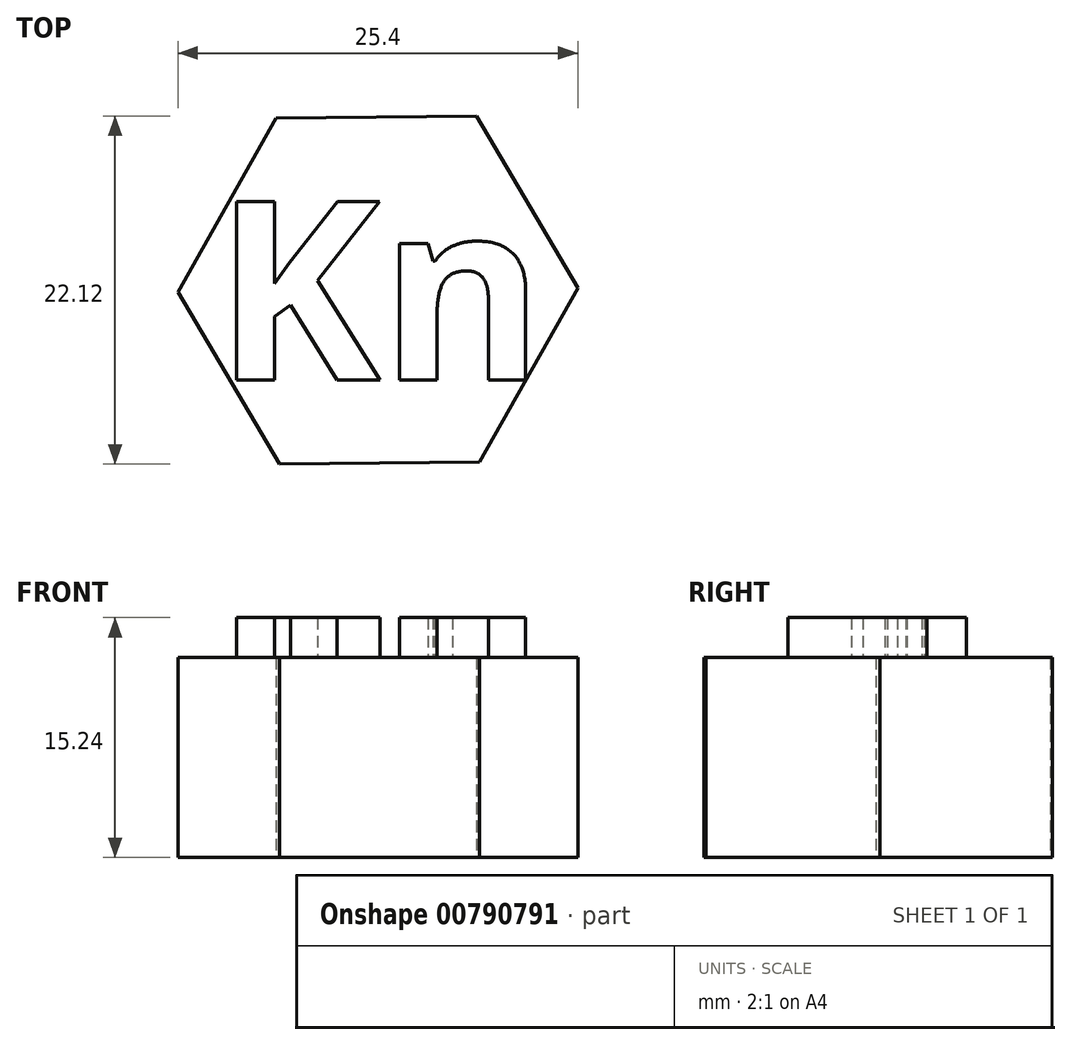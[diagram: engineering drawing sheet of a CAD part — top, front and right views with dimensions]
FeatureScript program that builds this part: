
annotation { "Feature Type Name" : "Feature", "Feature Type Description" : "" }
export const myFeature = defineFeature(function(context is Context, id is Id, definition is map)
    precondition{}
    {
        {
            var Q0;
            Q0=qCreatedBy(makeId("Top.planeOp"),FACE);
            var sketch = newSketch(context, id + "F0", { "sketchPlane" : qUnion([Q0])});
            skCircle(sketch, "E0.cCircle", {"center": v(0, 0) * mm, "radius": 11 * mm, "construction": true});
            skLineSegment(sketch, "E0.0", {"start": v(6.24, 11.06) * mm, "end": v(12.7, 0.13) * mm});
            skLineSegment(sketch, "E0.1", {"start": v(12.7, 0.13) * mm, "end": v(6.46, -10.94) * mm});
            skLineSegment(sketch, "E0.2", {"start": v(6.46, -10.94) * mm, "end": v(-6.24, -11.06) * mm});
            skLineSegment(sketch, "E0.3", {"start": v(-6.24, -11.06) * mm, "end": v(-12.7, -0.13) * mm});
            skLineSegment(sketch, "E0.4", {"start": v(-12.7, -0.13) * mm, "end": v(-6.46, 10.94) * mm});
            skLineSegment(sketch, "E0.5", {"start": v(-6.46, 10.94) * mm, "end": v(6.24, 11.06) * mm});
            skPoint(sketch, "E0.0.midPoint", {"position": v(9.47, 5.6) * mm});
            skSolve(sketch);
        }
        {
            var Q0;
            Q0=qSketchRegion(id+"F0",true);
            extrude(context, id + "F1", {"entities" : qUnion([Q0]), "depth" : 12.7 * mm, "offsetDistance" : 25.4 * mm});
        }
        {
            var Q0;
            Q0=makeQuery(id+"F1.opExtrude","CAP_FACE",FACE,{"disambiguationData":[OSD([sQuery(id+"F0.wireOp",EDGE,"E0.0"),sQuery(id+"F0.wireOp",EDGE,"E0.1"),sQuery(id+"F0.wireOp",EDGE,"E0.2"),sQuery(id+"F0.wireOp",EDGE,"E0.3"),sQuery(id+"F0.wireOp",EDGE,"E0.4"),sQuery(id+"F0.wireOp",EDGE,"E0.5")])],"isStart":false});
            var sketch = newSketch(context, id + "F2", { "sketchPlane" : qUnion([Q0])});
            skText(sketch, "E1", { "text": "Kn", "fontName": "OpenSans-Bold.ttf"});
            const initialGuessF2  = {"E1": [-0.0104, -0.00572, 1, 0, 0.01143]};
            skSetInitialGuess(sketch, initialGuessF2);
            skSolve(sketch);
        }
        {
            var Q0;
            Q0 = qSketchRegion(id + "F2", true);
            extrude(context, id + "F3", {"entities" : qUnion([Q0]), "operationType" : NewBodyOperationType.ADD, "depth" : 2.54 * mm, "offsetDistance" : 25.4 * mm});
        }
    });
